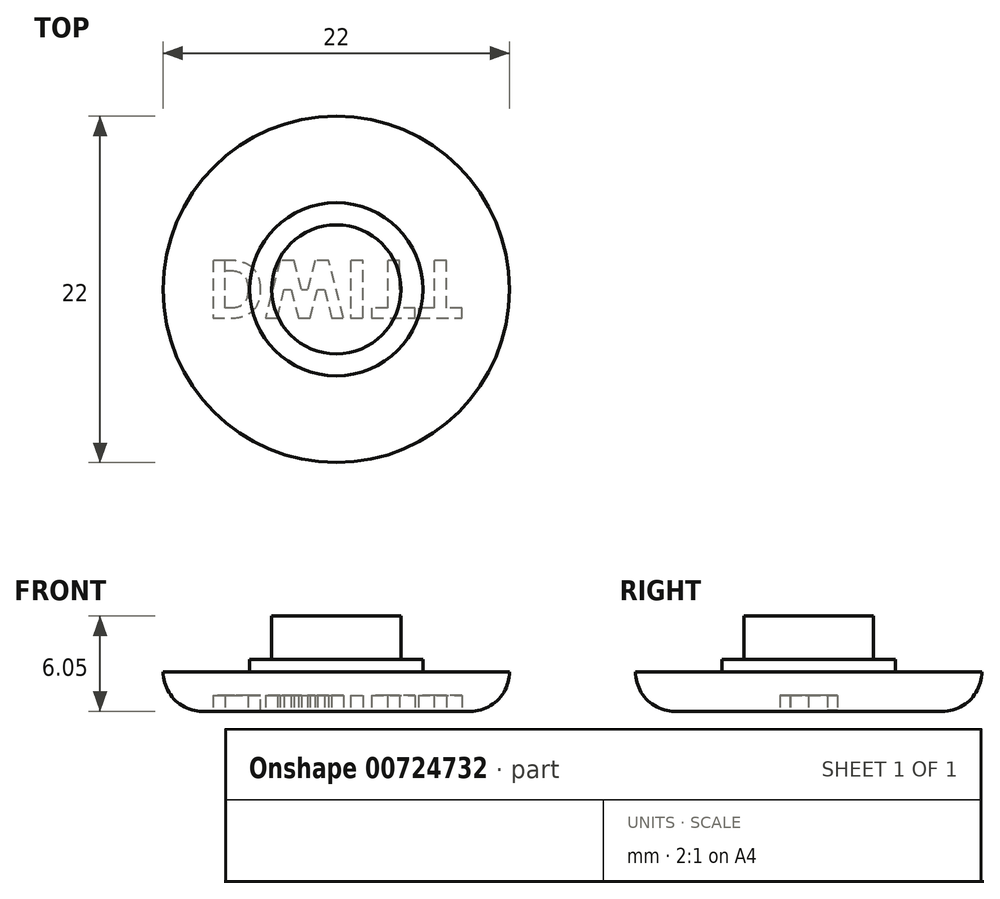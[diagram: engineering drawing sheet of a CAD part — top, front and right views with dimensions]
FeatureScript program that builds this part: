
annotation { "Feature Type Name" : "Feature", "Feature Type Description" : "" }
export const myFeature = defineFeature(function(context is Context, id is Id, definition is map)
    precondition{}
    {
        {
            var Q0;
            Q0=qCreatedBy(makeId("Top.planeOp"),FACE);
            var sketch = newSketch(context, id + "F0", { "sketchPlane" : qUnion([Q0])});
            skCircle(sketch, "E0", {"center": v(0, 0) * mm, "radius": 11 * mm});
            skCircle(sketch, "E1", {"center": v(0, 0) * mm, "radius": 4.1 * mm});
            skCircle(sketch, "E2", {"center": v(0, 0) * mm, "radius": 5.5 * mm});
            skSolve(sketch);
        }
        {
            var Q0;
            Q0=makeQuery(id+"F0.imprint","IMPRINT",FACE,{"disambiguationData":[TD([[makeQuery(id+"F0.imprint","IMPRINT",EDGE,{"derivedFrom":sQuery(id+"F0.wireOp",EDGE,"E0")}),1.0]])]});
            extrude(context, id + "F1", {"entities" : qUnion([Q0]), "depth" : 2.5 * mm, "offsetDistance" : 25 * mm});
        }
        {
            var Q0;
            Q0=makeQuery(id+"F0.imprint","IMPRINT",FACE,{"disambiguationData":[TD([[makeQuery(id+"F0.imprint","IMPRINT",EDGE,{"derivedFrom":sQuery(id+"F0.wireOp",EDGE,"E1")}),-1.0]])]});
            var Q1;
            Q1=makeQuery(id+"F1.opExtrude","CAP_FACE",FACE,{"disambiguationData":[OSD([sQuery(id+"F0.wireOp",EDGE,"E0"),sQuery(id+"F0.wireOp",EDGE,"E2")])],"isStart":false});
            extrude(context, id + "F2", {"entities" : qUnion([Q0]), "operationType" : NewBodyOperationType.ADD, "endBound" : BoundingType.UP_TO_SURFACE, "depth" : 25 * mm, "endBoundEntityFace" : qUnion([Q1]), "hasOffset" : true, "offsetDistance" : .8 * mm, "offsetOppositeDirection" : true});
        }
        {
            var Q0;
            Q0=makeQuery(id+"F0.imprint","IMPRINT",FACE,{"disambiguationData":[TD([[makeQuery(id+"F0.imprint","IMPRINT",EDGE,{"derivedFrom":sQuery(id+"F0.wireOp",EDGE,"E1")}),1.0]])]});
            var Q1;
            Q1=makeQuery(id+"F2.opExtrude","CAP_FACE",FACE,{"disambiguationData":[OSD([sQuery(id+"F0.wireOp",EDGE,"E0"),sQuery(id+"F0.wireOp",EDGE,"E2")])],"isStart":false});
            extrude(context, id + "F3", {"entities" : qUnion([Q0]), "operationType" : NewBodyOperationType.ADD, "endBound" : BoundingType.UP_TO_SURFACE, "depth" : 3 * mm, "endBoundEntityFace" : qUnion([Q1]), "hasOffset" : true, "offsetDistance" : 2.75 * mm, "offsetOppositeDirection" : true});
        }
        {
            var Q0;
            {var subQ0=sQuery(id+"F0.wireOp",EDGE,"E1");var subQ1=sQuery(id+"F0.wireOp",EDGE,"E2");Q0=makeQuery(id+"F3.boolean.opBoolean","MERGE",FACE,{"derivedFrom":[makeQuery(id+"F2.boolean.opBoolean","MERGE",FACE,{"derivedFrom":[makeQuery(id+"F1.opExtrude","CAP_FACE",FACE,{"disambiguationData":[OSD([sQuery(id+"F0.wireOp",EDGE,"E0"),subQ1])],"isStart":true}),makeQuery(id+"F2.opExtrude","CAP_FACE",FACE,{"disambiguationData":[OSD([subQ0,subQ1])],"isStart":true})]}),makeQuery(id+"F3.opExtrude","CAP_FACE",FACE,{"disambiguationData":[OSD([subQ0])],"isStart":true})]});}
            fillet(context, id + "F4", {"entities" : qUnion([Q0]), "radius" : 2.5 * mm, "tangentPropagation" : true, "allowEdgeOverflow" : false});
        }
        {
            var Q0;
            Q0=qCreatedBy(makeId("Right.planeOp"),FACE);
            var sketch = newSketch(context, id + "F5", { "sketchPlane" : qUnion([Q0])});
            skEllipse(sketch, "E3", {"center": v(-63.43, -1.89) * mm, "majorRadius": 11 * mm, "minorRadius": 2.5 * mm, "majorAxis": v(-1, 0)});
            skPoint(sketch, "E4", {"position": v(-63.43, 0.61) * mm});
            skLineSegment(sketch, "E5", {"start": v(-55.79, 0) * mm, "end": v(-71.08, 0) * mm});
            skArc(sketch, "E6", {"start": v(-11, 2.37) * mm, "mid": v(-6, 2.57) * mm, "end": v(-11, 2.5) * mm});
            skArc(sketch, "E7", {"start": v(6, 2.5) * mm, "mid": v(6, 2.46) * mm, "end": v(6, 2.42) * mm});
            skLineSegment(sketch, "E8", {"start": v(-63.43, 0.61) * mm, "end": v(-63.43, -4.39) * mm});
            skPoint(sketch, "E9.orphan", {"position": v(-63.43, -3.78) * mm});
            skPoint(sketch, "E10.orphan", {"position": v(-63.43, 0) * mm});
            skSolve(sketch);
        }
        {
            var Q0;
            {var subQ0=sQuery(id+"F0.wireOp",EDGE,"E1");var subQ1=sQuery(id+"F0.wireOp",EDGE,"E2");Q0=makeQuery(id+"F3.boolean.opBoolean","MERGE",FACE,{"derivedFrom":[makeQuery(id+"F2.boolean.opBoolean","MERGE",FACE,{"derivedFrom":[makeQuery(id+"F1.opExtrude","CAP_FACE",FACE,{"disambiguationData":[OSD([sQuery(id+"F0.wireOp",EDGE,"E0"),subQ1])],"isStart":true}),makeQuery(id+"F2.opExtrude","CAP_FACE",FACE,{"disambiguationData":[OSD([subQ0,subQ1])],"isStart":true})]}),makeQuery(id+"F3.opExtrude","CAP_FACE",FACE,{"disambiguationData":[OSD([subQ0])],"isStart":true})]});}
            var sketch = newSketch(context, id + "F6", { "sketchPlane" : qUnion([Q0])});
            skSolve(sketch);
        }
        {
            var Q0;
            {var subQ0=sQuery(id+"F0.wireOp",EDGE,"E1");var subQ1=sQuery(id+"F0.wireOp",EDGE,"E2");var subQ2=sQuery(id+"F0.wireOp",EDGE,"E0");Q0=makeQuery(id+"F6.imprint","IMPRINT",FACE,{"disambiguationData":[TD([[makeQuery(id+"F6.imprint","IMPRINT",EDGE,{"derivedFrom":makeQuery(id+"F4.opFillet","BLEND_EDGE",EDGE,{"blendedFrom":[makeQuery(id+"F1.opExtrude","CAP_EDGE",EDGE,{"disambiguationData":[OSD([subQ2])],"isStart":true}),makeQuery(id+"F3.boolean.opBoolean","MERGE",FACE,{"derivedFrom":[makeQuery(id+"F2.boolean.opBoolean","MERGE",FACE,{"derivedFrom":[makeQuery(id+"F1.opExtrude","CAP_FACE",FACE,{"disambiguationData":[OSD([subQ2,subQ1])],"isStart":true}),makeQuery(id+"F2.opExtrude","CAP_FACE",FACE,{"disambiguationData":[OSD([subQ0,subQ1])],"isStart":true})]}),makeQuery(id+"F3.opExtrude","CAP_FACE",FACE,{"disambiguationData":[OSD([subQ0])],"isStart":true})]})],"blendedInto":[makeQuery(id+"F3.boolean.opBoolean","MERGE",FACE,{"derivedFrom":[makeQuery(id+"F2.boolean.opBoolean","MERGE",FACE,{"derivedFrom":[makeQuery(id+"F1.opExtrude","CAP_FACE",FACE,{"disambiguationData":[OSD([subQ2,subQ1])],"isStart":true}),makeQuery(id+"F2.opExtrude","CAP_FACE",FACE,{"disambiguationData":[OSD([subQ0,subQ1])],"isStart":true})]}),makeQuery(id+"F3.opExtrude","CAP_FACE",FACE,{"disambiguationData":[OSD([subQ0])],"isStart":true})]})]})}),1.0]])]});}
            var sketch = newSketch(context, id + "F7", { "sketchPlane" : qUnion([Q0])});
            skLineSegment(sketch, "E11", {"start": v(-8.5, 0) * mm, "end": v(8.5, 0) * mm});
            skText(sketch, "E12", { "text": "DWITT", "fontName": "OpenSans-Bold.ttf"});
            const initialGuessF7  = {"E12": [-0.0083, -0.00184, 1, 0, 0.00369]};
            skSetInitialGuess(sketch, initialGuessF7);
            skSolve(sketch);
        }
        {
            var Q0;
            Q0=qSketchRegion(id+"F7",true);
            extrude(context, id + "F8", {"entities" : qUnion([Q0]), "operationType" : NewBodyOperationType.REMOVE, "oppositeDirection" : true, "depth" : 1 * mm, "offsetDistance" : 25 * mm});
        }
        {
            var Q0;
            {var subQ3=sQuery(id+"F0.wireOp",EDGE,"E0");var subQ8=sQuery(id+"F0.wireOp",EDGE,"E1");var subQ9=sQuery(id+"F0.wireOp",EDGE,"E2");Q0=makeQuery(id+"F8.boolean.opBoolean","SPLIT",FACE,{"disambiguationData":[TD([makeQuery(id+"F4.opFillet","BLEND_FACE",FACE,{"disambiguationData":[OSD([subQ3])]})])],"derivedFrom":makeQuery(id+"F3.boolean.opBoolean","MERGE",FACE,{"derivedFrom":[makeQuery(id+"F2.boolean.opBoolean","MERGE",FACE,{"derivedFrom":[makeQuery(id+"F1.opExtrude","CAP_FACE",FACE,{"disambiguationData":[OSD([subQ3,subQ9])],"isStart":true}),makeQuery(id+"F2.opExtrude","CAP_FACE",FACE,{"disambiguationData":[OSD([subQ8,subQ9])],"isStart":true})]}),makeQuery(id+"F3.opExtrude","CAP_FACE",FACE,{"disambiguationData":[OSD([subQ8])],"isStart":true})]})});}
            var sketch = newSketch(context, id + "F9", { "sketchPlane" : qUnion([Q0])});
            skLineSegment(sketch, "E13.bottom", {"start": v(-7.06, -1.2) * mm, "end": v(-7.06, -1.2) * mm});
            skLineSegment(sketch, "E13.top", {"start": v(-7.06, -1.84) * mm, "end": v(-7.06, -1.84) * mm});
            skLineSegment(sketch, "E13.left", {"start": v(-7.06, -1.2) * mm, "end": v(-7.06, -1.84) * mm});
            skLineSegment(sketch, "E13.right", {"start": v(-7.06, -1.2) * mm, "end": v(-7.06, -1.84) * mm});
            skSolve(sketch);
        }
        {
            var Q0;
            Q0=qSketchRegion(id+"F9",true);
            extrude(context, id + "F10", {"entities" : qUnion([Q0]), "operationType" : NewBodyOperationType.ADD, "oppositeDirection" : true, "depth" : .1 * mm, "offsetDistance" : 25 * mm});
        }
    });
